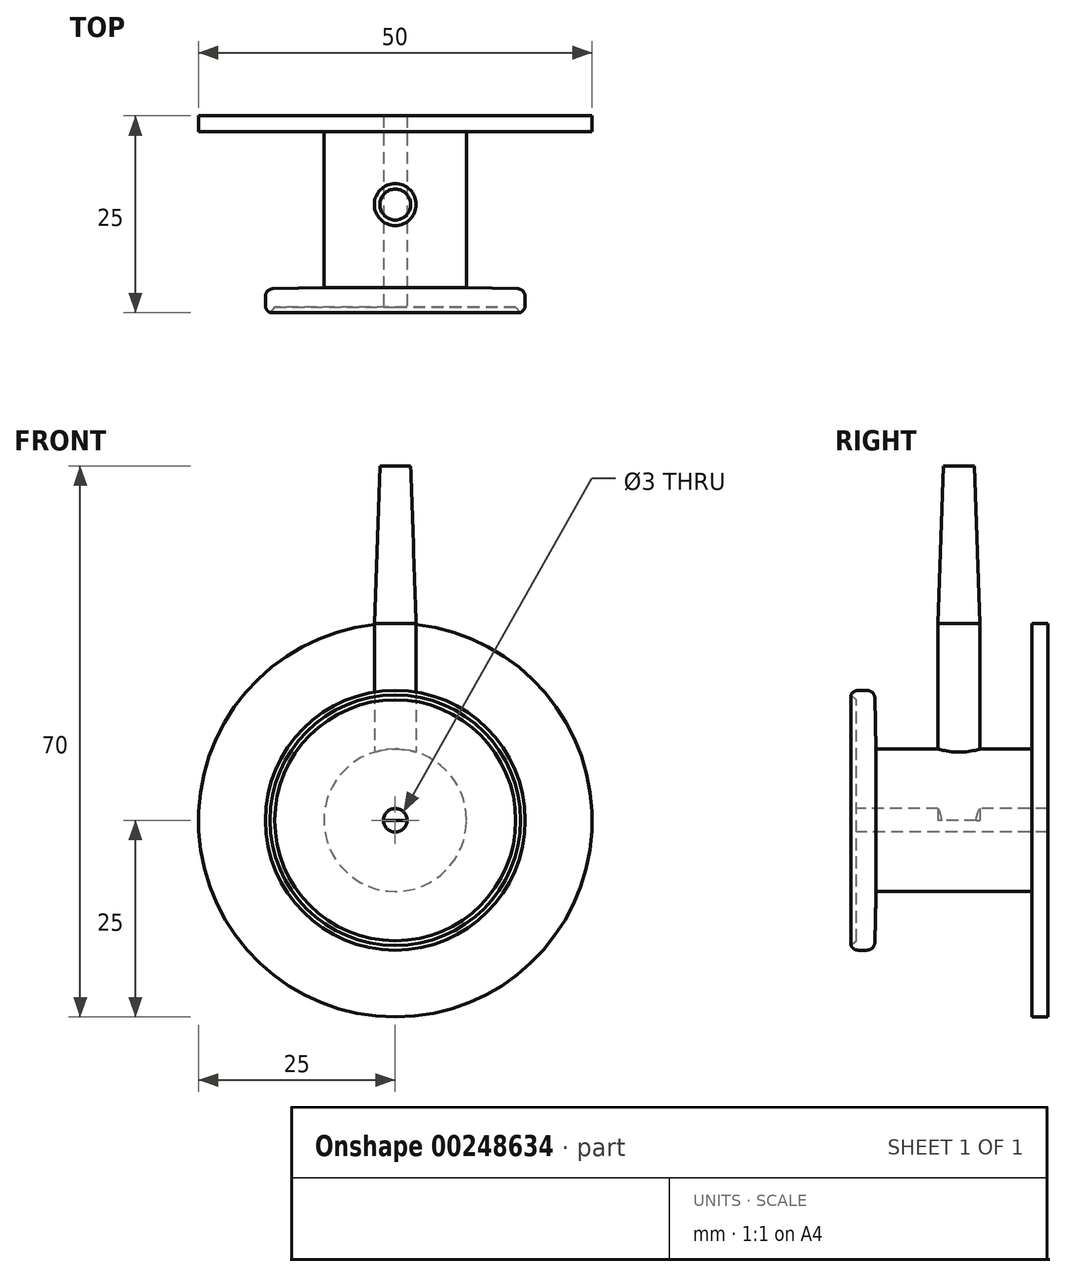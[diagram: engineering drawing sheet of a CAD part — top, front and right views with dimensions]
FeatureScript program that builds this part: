
annotation { "Feature Type Name" : "Feature", "Feature Type Description" : "" }
export const myFeature = defineFeature(function(context is Context, id is Id, definition is map)
    precondition{}
    {
        {
            var Q0;
            Q0=qCreatedBy(makeId("Top.planeOp"),FACE);
            var sketch = newSketch(context, id + "F0", { "sketchPlane" : qUnion([Q0])});
            skLineSegment(sketch, "E0", {"start": v(1.5, 21.81) * mm, "end": v(25, 21.81) * mm});
            skLineSegment(sketch, "E1", {"start": v(25, 21.81) * mm, "end": v(25, 19.81) * mm});
            skLineSegment(sketch, "E2", {"start": v(25, 19.81) * mm, "end": v(9.05, 19.81) * mm});
            skLineSegment(sketch, "E3", {"start": v(9.05, 19.81) * mm, "end": v(9.05, 0) * mm});
            skLineSegment(sketch, "E4", {"start": v(9.05, 0) * mm, "end": v(16.5, -0.19) * mm});
            skLineSegment(sketch, "E5", {"start": v(16.5, -0.19) * mm, "end": v(16.5, -3.19) * mm});
            skLineSegment(sketch, "E6", {"start": v(16.5, -3.19) * mm, "end": v(15.9, -3.19) * mm});
            skLineSegment(sketch, "E7", {"start": v(0, -3.19) * mm, "end": v(0, 21.81) * mm, "construction": true});
            skLineSegment(sketch, "E8", {"start": v(1.5, 21.81) * mm, "end": v(1.5, -2.48) * mm});
            skLineSegment(sketch, "E9", {"start": v(15.9, -3.19) * mm, "end": v(15.3, -2.48) * mm});
            skLineSegment(sketch, "E10", {"start": v(15.3, -2.48) * mm, "end": v(1.5, -2.48) * mm});
            skSolve(sketch);
        }
        {
            var Q0;
            Q0=makeQuery(id+"F0.imprint","IMPRINT",FACE,{"disambiguationData":[TD([[makeQuery(id+"F0.imprint","IMPRINT",EDGE,{"derivedFrom":sQuery(id+"F0.wireOp",EDGE,"E0")}),-1.0]])]});
            var Q1;
            Q1=sQuery(id+"F0.wireOp",EDGE,"E7");
            revolve(context, id + "F1", {"entities" : qUnion([Q0]), "axis" : qUnion([Q1]), "revolveType" : RevolveType.FULL});
        }
        {
            var Q0;
            Q0=makeQuery(id+"F1.opRevolve","SWEPT_EDGE",EDGE,{"disambiguationData":[OSD([sQuery(id+"F0.wireOp",EDGE,"E5"),sQuery(id+"F0.wireOp",EDGE,"E6")])]});
            var Q1;
            Q1=makeQuery(id+"F1.opRevolve","SWEPT_EDGE",EDGE,{"disambiguationData":[OSD([sQuery(id+"F0.wireOp",EDGE,"E4"),sQuery(id+"F0.wireOp",EDGE,"E5")])]});
            fillet(context, id + "F2", {"entities" : qUnion([Q0, Q1]), "radius" : 1 * mm, "tangentPropagation" : true, "allowEdgeOverflow" : false});
        }
        {
            var Q0;
            Q0=qCreatedBy(makeId("Top.planeOp"),FACE);
            var sketch = newSketch(context, id + "F3", { "sketchPlane" : qUnion([Q0])});
            skCircle(sketch, "E11", {"center": v(0, 10.53) * mm, "radius": 2.66 * mm});
            skSolve(sketch);
        }
        {
            var Q0;
            Q0 = qSketchRegion(id + "F3", true);
            extrude(context, id + "F4", {"entities" : qUnion([Q0]), "operationType" : NewBodyOperationType.ADD, "depth" : 45 * mm});
        }
        {
            var Q0;
            Q0=makeQuery(id+"F4.opExtrude","CAP_EDGE",EDGE,{"disambiguationData":[OSD([sQuery(id+"F3.wireOp",EDGE,"E11")])],"isStart":false});
            chamfer(context, id + "F5", {"entities" : qUnion([Q0]), "chamferType" : ChamferType.OFFSET_ANGLE, "width" : 20 * mm, "oppositeDirection" : true, "angle" : 2 * degree, "tangentPropagation" : true});
        }
    });
